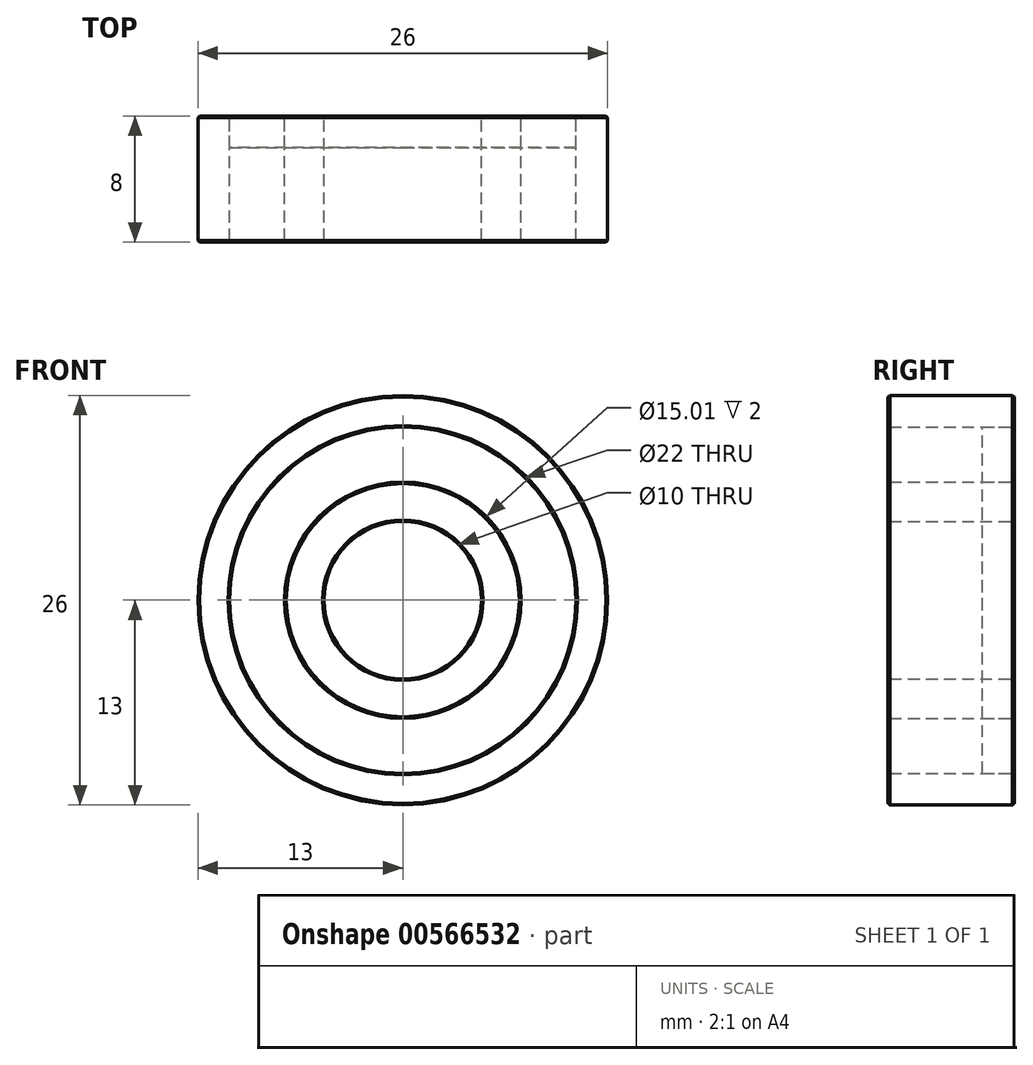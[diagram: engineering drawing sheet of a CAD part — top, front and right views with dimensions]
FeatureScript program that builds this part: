
annotation { "Feature Type Name" : "Feature", "Feature Type Description" : "" }
export const myFeature = defineFeature(function(context is Context, id is Id, definition is map)
    precondition{}
    {
        {
            var Q0;
            Q0=qCreatedBy(makeId("Front.planeOp"),FACE);
            var sketch = newSketch(context, id + "F0", { "sketchPlane" : qUnion([Q0])});
            skCircle(sketch, "E0", {"center": v(0, 0) * mm, "radius": 13 * mm});
            skCircle(sketch, "E1", {"center": v(0, 0) * mm, "radius": 11 * mm});
            skSolve(sketch);
        }
        {
            var Q0;
            Q0=qCreatedBy(makeId("Front.planeOp"),FACE);
            var sketch = newSketch(context, id + "F1", { "sketchPlane" : qUnion([Q0])});
            skCircle(sketch, "E2", {"center": v(0, 0) * mm, "radius": 7.5 * mm});
            skCircle(sketch, "E3", {"center": v(0, 0) * mm, "radius": 5 * mm});
            skSolve(sketch);
        }
        {
            var Q0;
            Q0 = qSketchRegion(id + "F0", true);
            extrude(context, id + "F2", {"entities" : qUnion([Q0]), "depth" : 8 * mm, "offsetDistance" : 25 * mm});
        }
        {
            var Q0;
            Q0 = qSketchRegion(id + "F1", true);
            extrude(context, id + "F3", {"entities" : qUnion([Q0]), "operationType" : NewBodyOperationType.ADD, "depth" : 8 * mm, "offsetDistance" : 25 * mm});
        }
        {
            var Q0;
            Q0=makeQuery(id+"F2.opExtrude","CAP_FACE",FACE,{"disambiguationData":[OSD([sQuery(id+"F0.wireOp",EDGE,"E0"),sQuery(id+"F0.wireOp",EDGE,"E1")])],"isStart":true});
            var Q1;
            Q1=makeQuery(id+"F3.opExtrude","CAP_FACE",FACE,{"disambiguationData":[OSD([sQuery(id+"F1.wireOp",EDGE,"E2"),sQuery(id+"F1.wireOp",EDGE,"E3")])],"isStart":true});
            var Q2;
            Q2=makeQuery(id+"F2.opExtrude","CAP_FACE",FACE,{"disambiguationData":[OSD([sQuery(id+"F0.wireOp",EDGE,"E0"),sQuery(id+"F0.wireOp",EDGE,"E1")])],"isStart":false});
            var Q3;
            Q3=makeQuery(id+"F3.opExtrude","CAP_FACE",FACE,{"disambiguationData":[OSD([sQuery(id+"F1.wireOp",EDGE,"E2"),sQuery(id+"F1.wireOp",EDGE,"E3")])],"isStart":false});
            chamfer(context, id + "F4", {"entities" : qUnion([Q0, Q1, Q2, Q3]), "width" : 0.1 * mm, "tangentPropagation" : true});
        }
        {
            var Q0;
            Q0=qCreatedBy(makeId("Front.planeOp"),FACE);
            var sketch = newSketch(context, id + "F5", { "sketchPlane" : qUnion([Q0])});
            skCircle(sketch, "E4", {"center": v(0, 0) * mm, "radius": 11 * mm});
            skCircle(sketch, "E5", {"center": v(0, 0) * mm, "radius": 7.5 * mm});
            skSolve(sketch);
        }
        {
            var Q0;
            Q0 = qSketchRegion(id + "F5", true);
            extrude(context, id + "F6", {"entities" : qUnion([Q0]), "depth" : 2 * mm, "offsetDistance" : 25 * mm});
        }
    });
